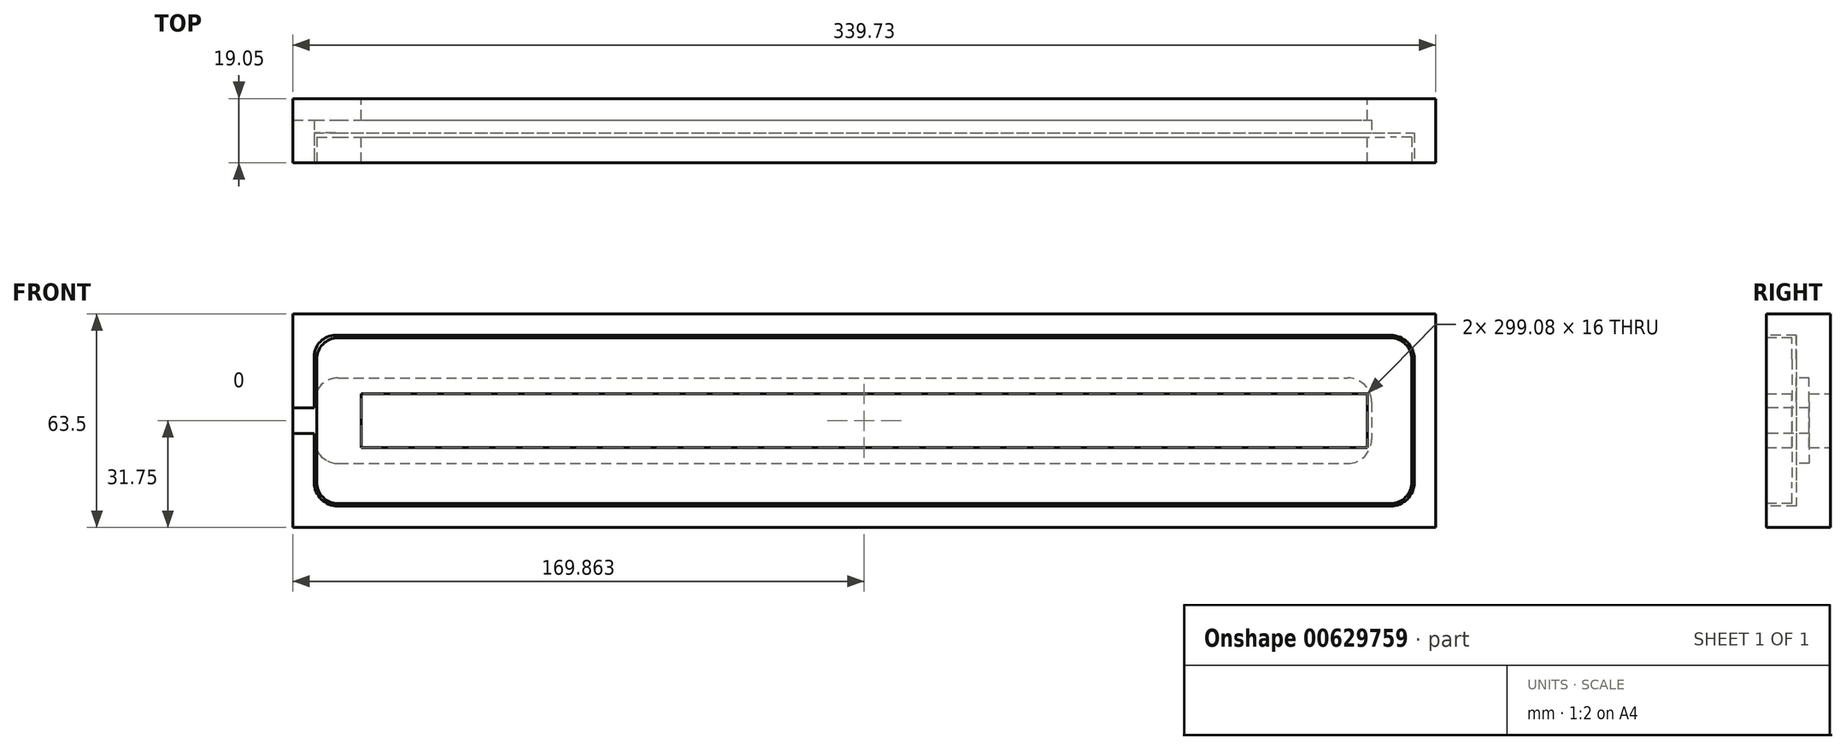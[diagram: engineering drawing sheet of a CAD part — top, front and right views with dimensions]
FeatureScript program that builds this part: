
annotation { "Feature Type Name" : "Feature", "Feature Type Description" : "" }
export const myFeature = defineFeature(function(context is Context, id is Id, definition is map)
    precondition{}
    {
        {
            var Q0;
            Q0=qCreatedBy(makeId("Front.planeOp"),FACE);
            var sketch = newSketch(context, id + "F0", { "sketchPlane" : qUnion([Q0])});
            skLineSegment(sketch, "E0.bottom", {"start": v(0, 0) * mm, "end": v(339.72, 0) * mm});
            skLineSegment(sketch, "E0.top", {"start": v(0, 63.5) * mm, "end": v(339.73, 63.5) * mm});
            skLineSegment(sketch, "E0.left", {"start": v(0, 0) * mm, "end": v(0, 63.5) * mm});
            skLineSegment(sketch, "E0.right", {"start": v(339.73, 0) * mm, "end": v(339.73, 63.5) * mm});
            skSolve(sketch);
        }
        {
            var Q0;
            Q0=makeQuery(id+"F0.imprint","IMPRINT",FACE,{"disambiguationData":[TD([[makeQuery(id+"F0.imprint","IMPRINT",EDGE,{"derivedFrom":sQuery(id+"F0.wireOp",EDGE,"E0.bottom")}),1.0]])]});
            extrude(context, id + "F1", {"entities" : qUnion([Q0]), "depth" : 19.05 * mm, "offsetDistance" : 25.4 * mm});
        }
        {
            var Q0;
            Q0=makeQuery(id+"F1.opExtrude","CAP_FACE",FACE,{"disambiguationData":[OSD([sQuery(id+"F0.wireOp",EDGE,"E0.bottom"),sQuery(id+"F0.wireOp",EDGE,"E0.top"),sQuery(id+"F0.wireOp",EDGE,"E0.left"),sQuery(id+"F0.wireOp",EDGE,"E0.right")])],"isStart":false});
            var sketch = newSketch(context, id + "F2", { "sketchPlane" : qUnion([Q0])});
            skLineSegment(sketch, "E1.bottom", {"start": v(13.46, 44.45) * mm, "end": v(313.56, 44.45) * mm});
            skLineSegment(sketch, "E1.top", {"start": v(13.46, 19.05) * mm, "end": v(313.56, 19.05) * mm});
            skLineSegment(sketch, "E1.left", {"start": v(6.35, 37.34) * mm, "end": v(6.35, 35.56) * mm});
            skLineSegment(sketch, "E1.right", {"start": v(320.68, 37.34) * mm, "end": v(320.68, 26.16) * mm});
            skLineSegment(sketch, "E2", {"start": v(6.35, 27.94) * mm, "end": v(0, 27.94) * mm});
            skLineSegment(sketch, "E3", {"start": v(0, 27.94) * mm, "end": v(0, 35.56) * mm});
            skLineSegment(sketch, "E4", {"start": v(0, 35.56) * mm, "end": v(6.35, 35.56) * mm});
            skLineSegment(sketch, "E5.trimOffspring", {"start": v(6.35, 27.94) * mm, "end": v(6.35, 26.16) * mm});
            skPoint(sketch, "E6.visualSharp", {"position": v(6.35, 44.45) * mm});
            skArc(sketch, "E6.filletArc", {"start": v(13.46, 44.45) * mm, "mid": v(8.43, 42.37) * mm, "end": v(6.35, 37.34) * mm});
            skPoint(sketch, "E7.visualSharp", {"position": v(6.35, 19.05) * mm});
            skArc(sketch, "E7.filletArc", {"start": v(6.35, 26.16) * mm, "mid": v(8.43, 21.13) * mm, "end": v(13.46, 19.05) * mm});
            skPoint(sketch, "E8.visualSharp", {"position": v(320.68, 44.45) * mm});
            skArc(sketch, "E8.filletArc", {"start": v(320.68, 37.34) * mm, "mid": v(318.6, 42.37) * mm, "end": v(313.56, 44.45) * mm});
            skPoint(sketch, "E9.visualSharp", {"position": v(320.68, 19.05) * mm});
            skArc(sketch, "E9.filletArc", {"start": v(313.56, 19.05) * mm, "mid": v(318.6, 21.13) * mm, "end": v(320.68, 26.16) * mm});
            skSolve(sketch);
        }
        {
            var Q0;
            Q0=makeQuery(id+"F2.imprint","IMPRINT",FACE,{"disambiguationData":[TD([[makeQuery(id+"F2.imprint","IMPRINT",EDGE,{"derivedFrom":sQuery(id+"F2.wireOp",EDGE,"E1.bottom")}),-1.0]])]});
            extrude(context, id + "F3", {"entities" : qUnion([Q0]), "operationType" : NewBodyOperationType.REMOVE, "oppositeDirection" : true, "depth" : 12.7 * mm, "offsetDistance" : 25.4 * mm});
        }
        {
            var Q0;
            Q0=makeQuery(id+"F1.opExtrude","CAP_FACE",FACE,{"disambiguationData":[OSD([sQuery(id+"F0.wireOp",EDGE,"E0.bottom"),sQuery(id+"F0.wireOp",EDGE,"E0.top"),sQuery(id+"F0.wireOp",EDGE,"E0.left"),sQuery(id+"F0.wireOp",EDGE,"E0.right")])],"isStart":false});
            var sketch = newSketch(context, id + "F4", { "sketchPlane" : qUnion([Q0])});
            skLineSegment(sketch, "E10.bottom", {"start": v(12.7, 57.15) * mm, "end": v(326.26, 57.15) * mm});
            skLineSegment(sketch, "E10.top", {"start": v(13.46, 6.35) * mm, "end": v(326.26, 6.35) * mm});
            skLineSegment(sketch, "E10.left", {"start": v(6.35, 50.8) * mm, "end": v(6.35, 13.46) * mm});
            skLineSegment(sketch, "E10.right", {"start": v(333.38, 50.04) * mm, "end": v(333.38, 13.46) * mm});
            skPoint(sketch, "E11.visualSharp", {"position": v(6.35, 57.15) * mm});
            skArc(sketch, "E11.filletArc", {"start": v(12.7, 57.15) * mm, "mid": v(8.2, 55.3) * mm, "end": v(6.35, 50.8) * mm});
            skPoint(sketch, "E12.visualSharp", {"position": v(6.35, 6.35) * mm});
            skArc(sketch, "E12.filletArc", {"start": v(6.35, 13.46) * mm, "mid": v(8.43, 8.43) * mm, "end": v(13.46, 6.35) * mm});
            skPoint(sketch, "E13.visualSharp", {"position": v(333.38, 6.35) * mm});
            skArc(sketch, "E13.filletArc", {"start": v(326.26, 6.35) * mm, "mid": v(331.3, 8.43) * mm, "end": v(333.38, 13.46) * mm});
            skPoint(sketch, "E14.visualSharp", {"position": v(333.38, 57.15) * mm});
            skArc(sketch, "E14.filletArc", {"start": v(333.38, 50.04) * mm, "mid": v(331.3, 55.07) * mm, "end": v(326.26, 57.15) * mm});
            skSolve(sketch);
        }
        {
            var Q0;
            {var subQ2=sQuery(id+"F4.wireOp",EDGE,"E10.bottom");Q0=makeQuery(id+"F4.imprint","IMPRINT",FACE,{"disambiguationData":[TD([[makeQuery(id+"F4.imprint","IMPRINT",EDGE,{"derivedFrom":subQ2}),-1.0]])]});}
            extrude(context, id + "F5", {"entities" : qUnion([Q0]), "operationType" : NewBodyOperationType.REMOVE, "oppositeDirection" : true, "depth" : 8.9 * mm, "offsetDistance" : 25.4 * mm});
        }
        {
            var Q0;
            Q0=makeQuery(id+"F1.opExtrude","CAP_FACE",FACE,{"disambiguationData":[OSD([sQuery(id+"F0.wireOp",EDGE,"E0.bottom"),sQuery(id+"F0.wireOp",EDGE,"E0.top"),sQuery(id+"F0.wireOp",EDGE,"E0.left"),sQuery(id+"F0.wireOp",EDGE,"E0.right")])],"isStart":false});
            var sketch = newSketch(context, id + "F6", { "sketchPlane" : qUnion([Q0])});
            skLineSegment(sketch, "E15.bottom", {"start": v(13.46, 56.39) * mm, "end": v(326.26, 56.39) * mm});
            skLineSegment(sketch, "E15.top", {"start": v(13.46, 7.11) * mm, "end": v(326.26, 7.11) * mm});
            skLineSegment(sketch, "E15.left", {"start": v(7.11, 50.04) * mm, "end": v(7.11, 13.46) * mm});
            skLineSegment(sketch, "E15.right", {"start": v(332.61, 50.04) * mm, "end": v(332.61, 13.46) * mm});
            skPoint(sketch, "E16.visualSharp", {"position": v(7.11, 7.11) * mm});
            skArc(sketch, "E16.filletArc", {"start": v(7.11, 13.46) * mm, "mid": v(8.97, 8.97) * mm, "end": v(13.46, 7.11) * mm});
            skPoint(sketch, "E17.visualSharp", {"position": v(7.11, 56.39) * mm});
            skArc(sketch, "E17.filletArc", {"start": v(13.46, 56.39) * mm, "mid": v(8.97, 54.53) * mm, "end": v(7.11, 50.04) * mm});
            skPoint(sketch, "E18.visualSharp", {"position": v(332.61, 56.39) * mm});
            skArc(sketch, "E18.filletArc", {"start": v(332.61, 50.04) * mm, "mid": v(330.75, 54.53) * mm, "end": v(326.26, 56.39) * mm});
            skPoint(sketch, "E19.visualSharp", {"position": v(332.61, 7.11) * mm});
            skArc(sketch, "E19.filletArc", {"start": v(326.26, 7.11) * mm, "mid": v(330.75, 8.97) * mm, "end": v(332.61, 13.46) * mm});
            skSolve(sketch);
        }
        {
            var Q0;
            Q0=makeQuery(id+"F6.imprint","IMPRINT",FACE,{"disambiguationData":[TD([[makeQuery(id+"F6.imprint","IMPRINT",EDGE,{"derivedFrom":sQuery(id+"F6.wireOp",EDGE,"E15.bottom")}),-1.0]])]});
            extrude(context, id + "F7", {"entities" : qUnion([Q0]), "depth" : -7.62 * mm, "offsetDistance" : 25.4 * mm});
        }
        {
            var Q0;
            Q0=makeQuery(id+"F1.opExtrude","CAP_FACE",FACE,{"disambiguationData":[OSD([sQuery(id+"F0.wireOp",EDGE,"E0.bottom"),sQuery(id+"F0.wireOp",EDGE,"E0.top"),sQuery(id+"F0.wireOp",EDGE,"E0.left"),sQuery(id+"F0.wireOp",EDGE,"E0.right")])],"isStart":true});
            var sketch = newSketch(context, id + "F8", { "sketchPlane" : qUnion([Q0])});
            skLineSegment(sketch, "E20.bottom", {"start": v(-319.4, 39.75) * mm, "end": v(-20.32, 39.75) * mm});
            skLineSegment(sketch, "E20.top", {"start": v(-319.4, 23.75) * mm, "end": v(-20.32, 23.75) * mm});
            skLineSegment(sketch, "E20.left", {"start": v(-319.4, 39.75) * mm, "end": v(-319.4, 23.75) * mm});
            skLineSegment(sketch, "E20.right", {"start": v(-20.32, 39.75) * mm, "end": v(-20.32, 23.75) * mm});
            skSolve(sketch);
        }
        {
            var Q0;
            Q0 = qSketchRegion(id + "F8", true);
            extrude(context, id + "F9", {"entities" : qUnion([Q0]), "operationType" : NewBodyOperationType.REMOVE, "oppositeDirection" : true, "depth" : 25.4 * mm, "offsetDistance" : 25.4 * mm});
        }
    });
